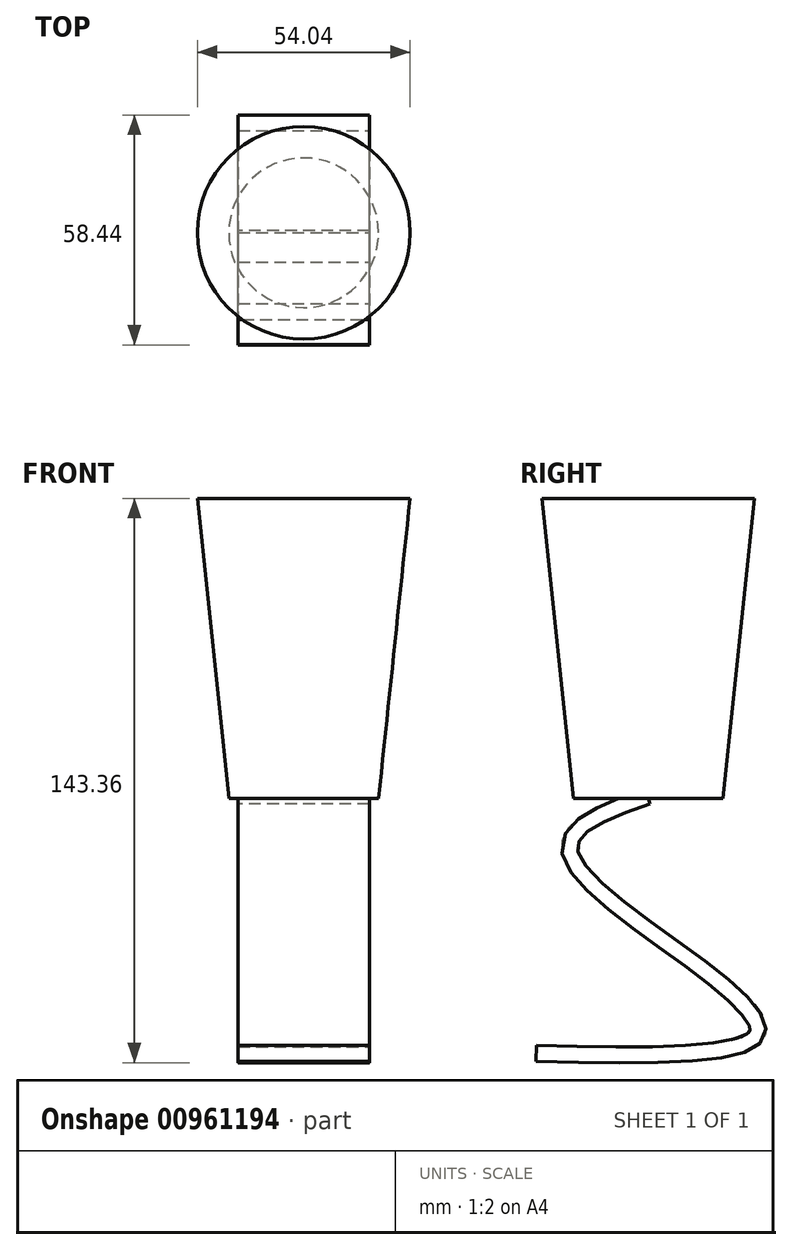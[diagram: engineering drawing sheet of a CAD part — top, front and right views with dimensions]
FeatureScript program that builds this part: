
annotation { "Feature Type Name" : "Feature", "Feature Type Description" : "" }
export const myFeature = defineFeature(function(context is Context, id is Id, definition is map)
    precondition{}
    {
        {
            var Q0;
            Q0=qCreatedBy(makeId("Top.planeOp"),FACE);
            var sketch = newSketch(context, id + "F0", { "sketchPlane" : qUnion([Q0])});
            skCircle(sketch, "E0", {"center": v(0, 0) * mm, "radius": 19 * mm});
            skSolve(sketch);
        }
        {
            var Q0;
            Q0=makeQuery(id+"F0.imprint","IMPRINT",FACE,{"disambiguationData":[TD([[makeQuery(id+"F0.imprint","IMPRINT",EDGE,{"derivedFrom":sQuery(id+"F0.wireOp",EDGE,"E0")}),1.0]])]});
            extrude(context, id + "F1", {"entities" : qUnion([Q0]), "depth" : 76.2 * mm, "offsetDistance" : 25.4 * mm, "hasDraft" : true, "draftAngle" : 6 * degree});
        }
        {
            var Q0;
            Q0=qCreatedBy(makeId("Right.planeOp"),FACE);
            var sketch = newSketch(context, id + "F2", { "sketchPlane" : qUnion([Q0])});
            skFitSpline(sketch, "E1", {"points": [v(0, 0) * mm, v(-19.44, -12.67) * mm, v(15.17, -43.77) * mm, v(27.97, -60.57) * mm, v(-28.47, -65.34) * mm], "startDerivative": vector(-145.73, -51.49) * mm, "endDerivative": vector(-248.9, 5.74) * mm});
            skSolve(sketch);
        }
        {
            var Q0;
            Q0=sQuery(id+"F2.wireOp",VERTEX,"E1.end");
            var Q1;
            Q1=sQuery(id+"F2.wireOp",EDGE,"E1");
            cPlane(context, id + "F3", {"entities" : qUnion([Q0, Q1]), "cplaneType" : CPlaneType.CURVE_POINT, "offset" : 25.4 * mm, "width" : 152.4 * mm, "height" : 152.4 * mm});
        }
        {
            var Q0;
            Q0=qCreatedBy(id+"F3.planeOp",FACE);
            var sketch = newSketch(context, id + "F4", { "sketchPlane" : qUnion([Q0])});
            skLineSegment(sketch, "E2.bottom", {"start": v(16.67, -67.43) * mm, "end": v(-16.67, -67.43) * mm});
            skLineSegment(sketch, "E2.top", {"start": v(16.67, -63.42) * mm, "end": v(-16.67, -63.42) * mm});
            skLineSegment(sketch, "E2.left", {"start": v(16.67, -67.43) * mm, "end": v(16.67, -63.42) * mm});
            skLineSegment(sketch, "E2.right", {"start": v(-16.67, -67.43) * mm, "end": v(-16.67, -63.42) * mm});
            skPoint(sketch, "E2.middle", {"position": v(0, -65.42) * mm});
            skSolve(sketch);
        }
        {
            var Q0;
            Q0=makeQuery(id+"F4.imprint","IMPRINT",FACE,{"disambiguationData":[TD([[makeQuery(id+"F4.imprint","IMPRINT",EDGE,{"derivedFrom":sQuery(id+"F4.wireOp",EDGE,"E2.bottom")}),-1.0]])]});
            var Q1;
            Q1=sQuery(id+"F2.wireOp",EDGE,"E1");
            sweep(context, id + "F5", {"operationType" : NewBodyOperationType.ADD, "profiles" : qUnion([Q0]), "path" : qUnion([Q1])});
        }
    });
